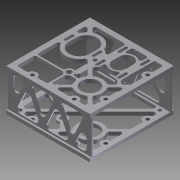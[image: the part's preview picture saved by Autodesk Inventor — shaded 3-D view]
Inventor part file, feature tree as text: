
AUTODESK INVENTOR PART (.ipt)
format: ipt  version: 2012 (Build 160160000, 160)  size: 936,448 bytes
history: native  units: in
note: dims shown in document units (in); Inventor stores cm internally (conversion verified against a paired STEP export)
features: thread x8, extrude x7, sketch x5, fillet x3, projected_geometry x1
ambient origin geometry x8: Origin, YZ Plane, XZ Plane, XY Plane, X Axis, Y Axis, Z Axis, Center Point
bodies: Solid1 (feature_tree)
feature tree (24):
  extrude  "Extrusion1"  Depth=0.1875in
  sketch  "Sketch2"  dims[d4=0.25in d5=0.25in d6=6.0in d7=0.0in]
  extrude  "Extrusion2"  Depth=6.0in TaperAngle=0.0deg
  extrude  "Extrusion3"  Depth=1.25in
  extrude  "Extrusion4"  Depth=0.375in
  fillet  "Fillet2"  Radius=0.875in
  sketch  "Sketch6"  dims[d21=0.125in d22=0.25in d24=0.25in d25=0.125in d27=0.125in d32=0.25in d33=0.0in d35=0.375in d36=0.375in d37=0.375in d38=0.375in d39=0.1719in d40=0.3438in d41=0.3438in d42=0.3438in d43=0.3438in d44=0.125in d46=0.125in d49=0.125in d50=0.125in d51=0.125in d52=0.125in d53=0.125in d54=0.125in d55=0.125in d56=0.125in d57=0.25in d58=0.0in d60=0.3798in d61=0.287in d62=0.287in d63=0.287in d64=0.125in d65=0.125in d66=0.125in d67=0.125in d68=0.125in d69=0.125in d70=0.125in d71=0.125in d72=0.125in d73=0.125in d74=0.375in d76=0.25in d77=0.375in d78=0.375in d79=0.25in d80=0.0in d81=0.25in d88=0.125in d89=1.25in d90=1.75in d91=0.75in d92=0.5in d94=0.2in d97=1.0in d98=0.5in d99=0.5in d102=0.2in d103=0.8in d104=0.8in d105=0.7874in d107=1.6in d108=0.7874in d110=1.6in d114=1.0in d115=1.0in d116=1.5in d117=1.0in d119=0.2in d122=3.25in d123=1.3125in d124=0.366in d126=1.75in d127=0.25in d128=0.0in d129=0.375in d131=3.5in d132=0.125in d153=0.25in d154=0.125in d156=0.375in d157=0.375in d160=0.25in d161=0.125in d162=0.25in d163=0.125in d165=0.875in d166=0.125in d168=0.3125in d169=0.125in d170=0.125in d171=1.0in d172=0.25in d178=0.45in d179=0.25in d180=0.0in d181=0.125in d183=0.25in d185=0.25in d186=0.125in d188=1.5625in d191=0.366in d193=0.25in d194=0.125in d197=0.875in d198=1.176in d199=0.1in d200=0.0in d201=0.0625in d203=0.25in d207=2.375in d208=1.75in d211=0.125in d213=0.375in d214=0.25in d215=0.3125in d220=0.375in d221=1.5in d222=0.25in d224=0.125in d225=1.75in d226=0.35in d227=0.25in d228=1.5in d229=1.5in d230=0.6705in d231=0.25in d232=1.5in d235=2.25in d236=0.25in d237=1.5in d238=0.3125in d239=0.7874in d241=3.0in d242=0.3937in d244=1.0in d246=1.5in d247=0.7874in d249=3.0in d250=0.3937in d252=1.0in d254=0.5in d255=0.25in d256=0.3125in d257=0.25in d258=0.5in d259=0.3125in d260=0.25in d262=0.625in d264=6.0in d267=0.25in d269=3.0in d270=6.0in d272=0.25in d273=0.125in d274=0.125in d275=0.1435in d276=2.0in d277=1.0in d278=0.0in d279=1.0in d280=0.0in d281=1.0in d282=0.0in d283=1.0in d284=0.0in d285=1.0in d286=0.0in d287=1.0in d288=0.0in d289=1.0in d290=0.0in d291=1.0in d292=0.0in d293=0.125in d294=0.125in d296=0.625in d297=0.25in d298=0.0625in d299=0.125in d300=0.5in d301=1.3125in d302=0.375in d303=0.375in d304=0.225in d306=0.0938in d307=0.1875in d308=1.0in d310=0.125in d311=1.0625in]
  fillet  "Fillet3"  Radius=0.25in
  extrude  "Extrusion5"  Depth=0.25in
  extrude  "Extrusion6"  Depth=0.25in
  fillet  "Fillet4"  Radius=0.125in
  extrude  "Extrusion7"  Depth=0.125in
  thread  "Thread1"  [1 undecoded]
  thread  "Thread2"  [1 undecoded]
  thread  "Thread3"  [1 undecoded]
  thread  "Thread4"  [1 undecoded]
  thread  "Thread5"  [1 undecoded]
  thread  "Thread6"  [1 undecoded]
  thread  "Thread7"  [1 undecoded]
  thread  "Thread8"  [1 undecoded]
  sketch  "Sketch1"  dims[d1=3.0in d2=0.1875in d3=0.25in]
  sketch  "Sketch4"  dims[d11=1.75in d13=1.25in]
  sketch  "Sketch5"  dims[d15=2.625in d16=1.5in d18=0.375in d19=0.875in d20=0.25in]
  projected_geometry  "Projected Loop1"
note: 8 required parameter values undecoded (feature->parameter linkage not recoverable at this tier; creation-order binding heuristic only, values carry confidence <= 0.55)
